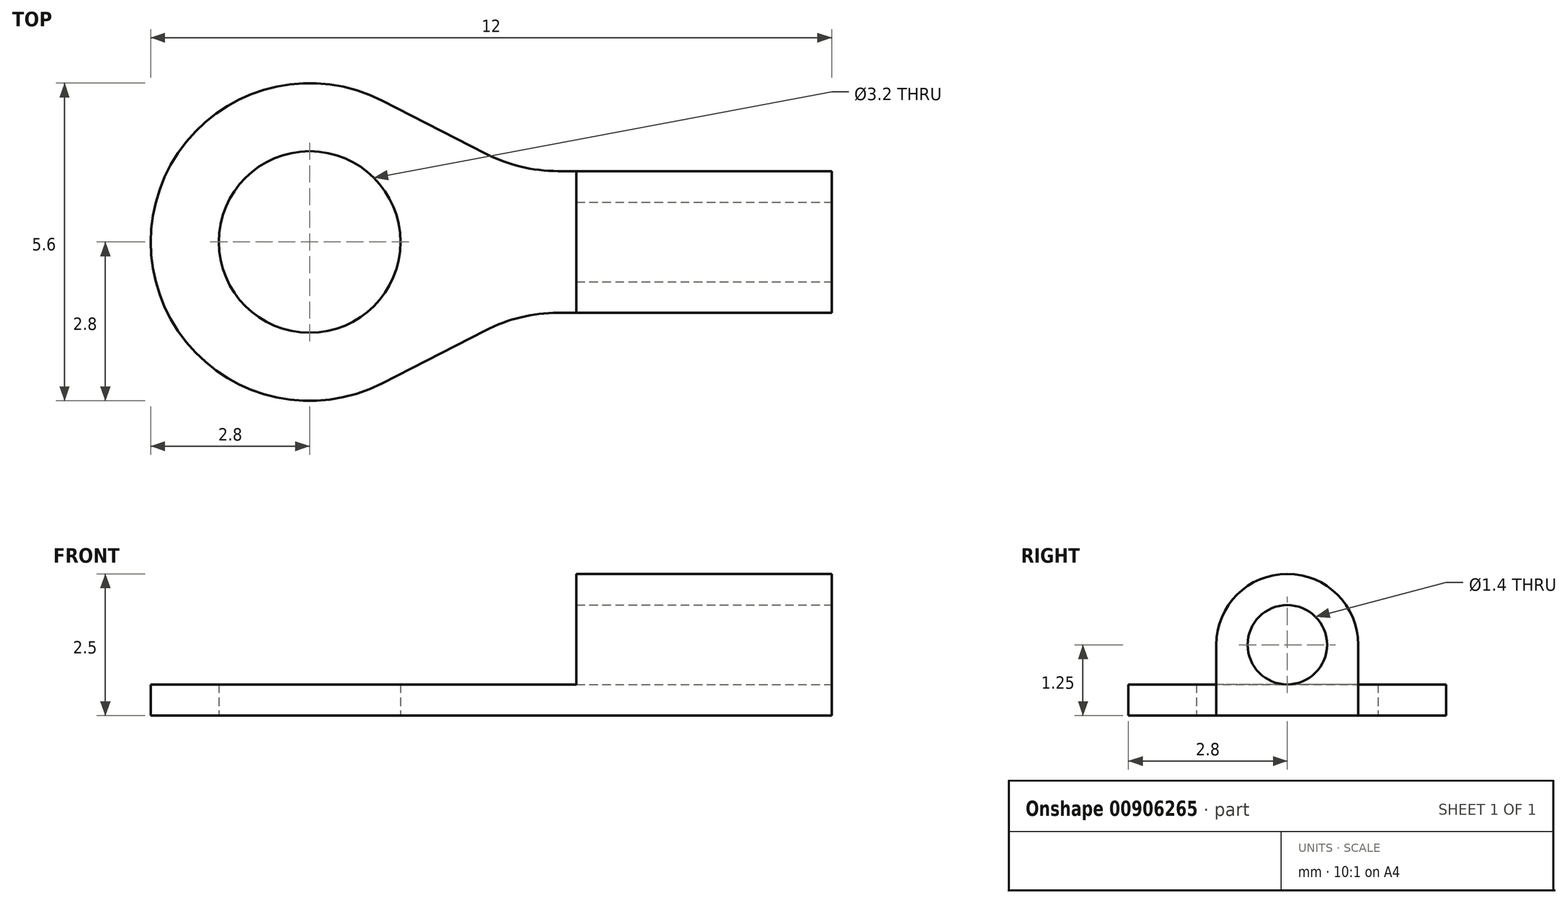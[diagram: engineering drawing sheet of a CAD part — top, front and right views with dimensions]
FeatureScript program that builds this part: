
annotation { "Feature Type Name" : "Feature", "Feature Type Description" : "" }
export const myFeature = defineFeature(function(context is Context, id is Id, definition is map)
    precondition{}
    {
        {
            var Q0;
            Q0=qCreatedBy(makeId("Top.planeOp"),FACE);
            var sketch = newSketch(context, id + "F0", { "sketchPlane" : qUnion([Q0])});
            skLineSegment(sketch, "E0", {"start": v(12, 1.55) * mm, "end": v(12, 4.05) * mm});
            skLineSegment(sketch, "E1", {"start": v(0, 2.8) * mm, "end": v(0, 2.8) * mm});
            skPoint(sketch, "E2.visualSharp", {"position": v(0, 5.6) * mm});
            skArc(sketch, "E2.filletArc", {"start": v(2.8, 5.6) * mm, "mid": v(0.82, 4.78) * mm, "end": v(0, 2.8) * mm});
            skPoint(sketch, "E3.visualSharp", {"position": v(0, 0) * mm});
            skArc(sketch, "E3.filletArc", {"start": v(0, 2.8) * mm, "mid": v(0.82, 0.82) * mm, "end": v(2.8, 0) * mm});
            skLineSegment(sketch, "E4.0", {"start": v(6.5, 1.47) * mm, "end": v(6.5, 1.55) * mm});
            skLineSegment(sketch, "E5.0", {"start": v(2.8, 0) * mm, "end": v(2.8, 5.6) * mm});
            skLineSegment(sketch, "E6.0", {"start": v(12, 4.05) * mm, "end": v(7.18, 4.05) * mm});
            skLineSegment(sketch, "E7.0", {"start": v(12, 1.55) * mm, "end": v(7.18, 1.55) * mm});
            skArc(sketch, "E8", {"start": v(4.08, 5.3) * mm, "mid": v(0, 2.8) * mm, "end": v(4.08, 0.3) * mm});
            skLineSegment(sketch, "E9", {"start": v(5.9, 4.36) * mm, "end": v(4.08, 5.3) * mm});
            skLineSegment(sketch, "E10", {"start": v(5.9, 1.24) * mm, "end": v(4.08, 0.3) * mm});
            skPoint(sketch, "E11.visualSharp", {"position": v(6.5, 4.05) * mm});
            skArc(sketch, "E11.filletArc", {"start": v(5.9, 4.36) * mm, "mid": v(6.52, 4.13) * mm, "end": v(7.18, 4.05) * mm});
            skPoint(sketch, "E12.visualSharp", {"position": v(6.5, 1.55) * mm});
            skArc(sketch, "E12.filletArc", {"start": v(7.18, 1.55) * mm, "mid": v(6.52, 1.47) * mm, "end": v(5.9, 1.24) * mm});
            skCircle(sketch, "E13", {"center": v(2.8, 2.8) * mm, "radius": 1.6 * mm});
            skPoint(sketch, "E14.orphan", {"position": v(12, 5.6) * mm});
            skPoint(sketch, "E15.orphan", {"position": v(12, 0) * mm});
            skPoint(sketch, "E16.orphan", {"position": v(6.5, 0) * mm});
            skPoint(sketch, "E17.start.orphan", {"position": v(6.5, 5.6) * mm});
            skLineSegment(sketch, "E18.trimOffspring", {"start": v(6.5, 4.05) * mm, "end": v(6.5, 4.13) * mm});
            skPoint(sketch, "E19.end.orphan", {"position": v(6.5, 2.8) * mm});
            skPoint(sketch, "E19.start.orphan", {"position": v(12, 2.8) * mm});
            skSolve(sketch);
        }
        {
            var Q0;
            Q0 = qSketchRegion(id + "F0", true);
            extrude(context, id + "F1", {"entities" : qUnion([Q0]), "depth" : 0.55 * mm, "offsetDistance" : 25 * mm});
        }
        {
            var Q0;
            Q0=makeQuery(id+"F1.opExtrude","CAP_FACE",FACE,{"disambiguationData":[OSD([sQuery(id+"F0.wireOp",EDGE,"E0"),sQuery(id+"F0.wireOp",EDGE,"E6.0"),sQuery(id+"F0.wireOp",EDGE,"E7.0"),sQuery(id+"F0.wireOp",EDGE,"E8"),sQuery(id+"F0.wireOp",EDGE,"E9"),sQuery(id+"F0.wireOp",EDGE,"E10"),sQuery(id+"F0.wireOp",EDGE,"E11.filletArc"),sQuery(id+"F0.wireOp",EDGE,"E12.filletArc"),sQuery(id+"F0.wireOp",EDGE,"E13")])],"isStart":false});
            var sketch = newSketch(context, id + "F2", { "sketchPlane" : qUnion([Q0])});
            skLineSegment(sketch, "E20.bottom", {"start": v(12, 4.05) * mm, "end": v(7.5, 4.05) * mm});
            skLineSegment(sketch, "E20.top", {"start": v(12, 1.55) * mm, "end": v(7.5, 1.55) * mm});
            skLineSegment(sketch, "E20.left", {"start": v(12, 4.05) * mm, "end": v(12, 1.55) * mm});
            skLineSegment(sketch, "E20.right", {"start": v(7.5, 4.05) * mm, "end": v(7.5, 1.55) * mm});
            skSolve(sketch);
        }
        {
            var Q0;
            Q0=makeQuery(id+"F2.imprint","IMPRINT",FACE,{"disambiguationData":[TD([[makeQuery(id+"F2.imprint","IMPRINT",EDGE,{"derivedFrom":sQuery(id+"F2.wireOp",EDGE,"E20.bottom")}),1.0]])]});
            extrude(context, id + "F3", {"entities" : qUnion([Q0]), "operationType" : NewBodyOperationType.ADD, "depth" : 1.95 * mm, "offsetDistance" : 25 * mm});
        }
        {
            var Q0;
            Q0=makeQuery(id+"F3.opExtrude","CAP_EDGE",EDGE,{"disambiguationData":[OSD([sQuery(id+"F2.wireOp",EDGE,"E20.top")])],"isStart":false});
            var Q1;
            Q1=makeQuery(id+"F3.opExtrude","CAP_EDGE",EDGE,{"disambiguationData":[OSD([sQuery(id+"F2.wireOp",EDGE,"E20.bottom")])],"isStart":false});
            fillet(context, id + "F4", {"entities" : qUnion([Q0, Q1]), "radius" : 1.25 * mm, "tangentPropagation" : true, "allowEdgeOverflow" : false});
        }
        {
            var Q0;
            Q0=makeQuery(id+"F3.boolean.opBoolean","MERGE",FACE,{"derivedFrom":[makeQuery(id+"F1.opExtrude","SWEPT_FACE",FACE,{"disambiguationData":[OSD([sQuery(id+"F0.wireOp",EDGE,"E0")])]}),makeQuery(id+"F3.opExtrude","SWEPT_FACE",FACE,{"disambiguationData":[OSD([sQuery(id+"F2.wireOp",EDGE,"E20.left")])]})]});
            var sketch = newSketch(context, id + "F5", { "sketchPlane" : qUnion([Q0])});
            skCircle(sketch, "E21", {"center": v(2.8, 1.25) * mm, "radius": 0.7 * mm});
            skSolve(sketch);
        }
        {
            var Q0;
            Q0=makeQuery(id+"F5.imprint","IMPRINT",FACE,{"disambiguationData":[TD([[makeQuery(id+"F5.imprint","IMPRINT",EDGE,{"derivedFrom":sQuery(id+"F5.wireOp",EDGE,"E21")}),1.0]])]});
            extrude(context, id + "F6", {"entities" : qUnion([Q0]), "operationType" : NewBodyOperationType.REMOVE, "oppositeDirection" : true, "depth" : 25 * mm, "offsetDistance" : 25 * mm});
        }
    });
